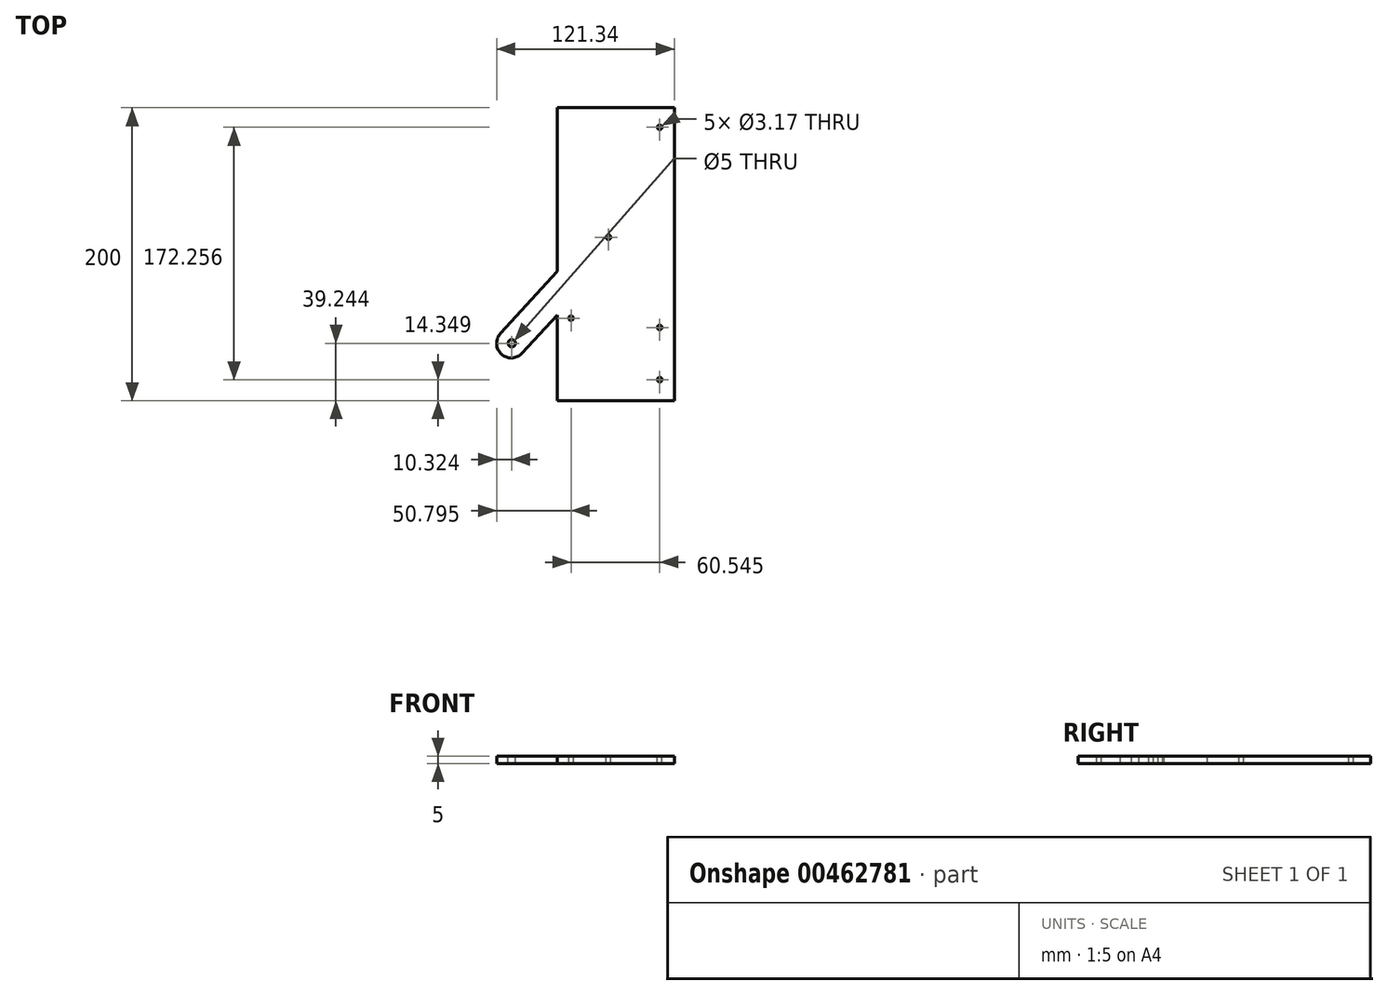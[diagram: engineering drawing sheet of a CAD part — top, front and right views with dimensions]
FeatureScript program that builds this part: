
annotation { "Feature Type Name" : "Feature", "Feature Type Description" : "" }
export const myFeature = defineFeature(function(context is Context, id is Id, definition is map)
    precondition{}
    {
        {
            var Q0;
            Q0=qCreatedBy(makeId("Top.planeOp"),FACE);
            var sketch = newSketch(context, id + "F0", { "sketchPlane" : qUnion([Q0])});
            skLineSegment(sketch, "E0.bottom", {"start": v(100, 150) * mm, "end": v(-100, 150) * mm});
            skLineSegment(sketch, "E0.top", {"start": v(100, -150) * mm, "end": v(-100, -150) * mm});
            skLineSegment(sketch, "E0.left", {"start": v(100, 150) * mm, "end": v(100, -150) * mm});
            skLineSegment(sketch, "E0.right", {"start": v(-100, 150) * mm, "end": v(-100, -150) * mm});
            skPoint(sketch, "E0.middle", {"position": v(0, 0) * mm});
            skSolve(sketch);
        }
        {
            var Q0;
            Q0=qSketchRegion(id+"F0",true);
            extrude(context, id + "F1", {"entities" : qUnion([Q0]), "depth" : 5 * mm});
        }
        {
            var Q0;
            Q0=makeQuery(id+"F1.opExtrude","CAP_FACE",FACE,{"disambiguationData":[OSD([sQuery(id+"F0.wireOp",EDGE,"E0.bottom"),sQuery(id+"F0.wireOp",EDGE,"E0.top"),sQuery(id+"F0.wireOp",EDGE,"E0.left"),sQuery(id+"F0.wireOp",EDGE,"E0.right")])],"isStart":false});
            var sketch = newSketch(context, id + "F2", { "sketchPlane" : qUnion([Q0])});
            skCircle(sketch, "E1", {"center": v(0, 0) * mm, "radius": 1.59 * mm});
            skCircle(sketch, "E2", {"center": v(0, -35.65) * mm, "radius": 1.59 * mm});
            skCircle(sketch, "E3", {"center": v(-60.54, 6.35) * mm, "radius": 1.59 * mm});
            skCircle(sketch, "E4", {"center": v(-35, 61.6) * mm, "radius": 1.59 * mm});
            skCircle(sketch, "E5", {"center": v(0, 136.6) * mm, "radius": 1.59 * mm});
            skLineSegment(sketch, "E6", {"start": v(0, 0) * mm, "end": v(-73.74, 0) * mm, "construction": true});
            skSolve(sketch);
        }
        {
            var Q0;
            Q0 = qSketchRegion(id + "F2", true);
            extrude(context, id + "F3", {"entities" : qUnion([Q0]), "operationType" : NewBodyOperationType.REMOVE, "endBound" : BoundingType.THROUGH_ALL, "oppositeDirection" : true, "depth" : 25 * mm});
        }
        {
            var Q0;
            Q0=makeQuery(id+"F1.opExtrude","CAP_FACE",FACE,{"disambiguationData":[OSD([sQuery(id+"F0.wireOp",EDGE,"E0.bottom"),sQuery(id+"F0.wireOp",EDGE,"E0.top"),sQuery(id+"F0.wireOp",EDGE,"E0.left"),sQuery(id+"F0.wireOp",EDGE,"E0.right")])],"isStart":false});
            var sketch = newSketch(context, id + "F4", { "sketchPlane" : qUnion([Q0])});
            skLineSegment(sketch, "E7.bottom", {"start": v(-70, 150) * mm, "end": v(10, 150) * mm});
            skLineSegment(sketch, "E7.top", {"start": v(-70, -50) * mm, "end": v(10, -50) * mm});
            skLineSegment(sketch, "E7.left", {"start": v(-70, 150) * mm, "end": v(-70, -50) * mm});
            skLineSegment(sketch, "E7.right", {"start": v(10, 150) * mm, "end": v(10, -50) * mm});
            skLineSegment(sketch, "E8.bottom", {"start": v(-100, 150) * mm, "end": v(100, 150) * mm});
            skLineSegment(sketch, "E8.top", {"start": v(-100, -150) * mm, "end": v(100, -150) * mm});
            skLineSegment(sketch, "E8.left", {"start": v(-100, 150) * mm, "end": v(-100, -150) * mm});
            skLineSegment(sketch, "E8.right", {"start": v(100, 150) * mm, "end": v(100, -150) * mm});
            skSolve(sketch);
        }
        {
            var Q0;
            Q0=makeQuery(id+"F4.imprint","IMPRINT",FACE,{"disambiguationData":[TD([[makeQuery(id+"F4.imprint","IMPRINT",EDGE,{"derivedFrom":sQuery(id+"F4.wireOp",EDGE,"E7.top")}),-1.0]])]});
            var Q1;
            Q1=makeQuery(id+"F4.imprint","IMPRINT",FACE,{"disambiguationData":[TD([[makeQuery(id+"F4.imprint","IMPRINT",EDGE,{"derivedFrom":makeQuery(id+"F3.boolean.opBoolean","COPY",EDGE,{"derivedFrom":makeQuery(id+"F3.opExtrude","CAP_EDGE",EDGE,{"disambiguationData":[OSD([sQuery(id+"F2.wireOp",EDGE,"E1")])],"isStart":true})})}),1.0]])]});
            var Q2;
            Q2=makeQuery(id+"F4.imprint","IMPRINT",FACE,{"disambiguationData":[TD([[makeQuery(id+"F4.imprint","IMPRINT",EDGE,{"derivedFrom":makeQuery(id+"F3.boolean.opBoolean","COPY",EDGE,{"derivedFrom":makeQuery(id+"F3.opExtrude","CAP_EDGE",EDGE,{"disambiguationData":[OSD([sQuery(id+"F2.wireOp",EDGE,"E2")])],"isStart":true})})}),1.0]])]});
            var Q3;
            Q3=makeQuery(id+"F4.imprint","IMPRINT",FACE,{"disambiguationData":[TD([[makeQuery(id+"F4.imprint","IMPRINT",EDGE,{"derivedFrom":makeQuery(id+"F3.boolean.opBoolean","COPY",EDGE,{"derivedFrom":makeQuery(id+"F3.opExtrude","CAP_EDGE",EDGE,{"disambiguationData":[OSD([sQuery(id+"F2.wireOp",EDGE,"E3")])],"isStart":true})})}),1.0]])]});
            var Q4;
            Q4=makeQuery(id+"F4.imprint","IMPRINT",FACE,{"disambiguationData":[TD([[makeQuery(id+"F4.imprint","IMPRINT",EDGE,{"derivedFrom":makeQuery(id+"F3.boolean.opBoolean","COPY",EDGE,{"derivedFrom":makeQuery(id+"F3.opExtrude","CAP_EDGE",EDGE,{"disambiguationData":[OSD([sQuery(id+"F2.wireOp",EDGE,"E4")])],"isStart":true})})}),1.0]])]});
            var Q5;
            Q5=makeQuery(id+"F4.imprint","IMPRINT",FACE,{"disambiguationData":[TD([[makeQuery(id+"F4.imprint","IMPRINT",EDGE,{"derivedFrom":makeQuery(id+"F3.boolean.opBoolean","COPY",EDGE,{"derivedFrom":makeQuery(id+"F3.opExtrude","CAP_EDGE",EDGE,{"disambiguationData":[OSD([sQuery(id+"F2.wireOp",EDGE,"E5")])],"isStart":true})})}),1.0]])]});
            extrude(context, id + "F5", {"entities" : qUnion([Q0, Q1, Q2, Q3, Q4, Q5]), "operationType" : NewBodyOperationType.REMOVE, "oppositeDirection" : true, "depth" : 25 * mm});
        }
        {
            var Q0;
            Q0=makeQuery(id+"F1.opExtrude","CAP_FACE",FACE,{"disambiguationData":[OSD([sQuery(id+"F0.wireOp",EDGE,"E0.bottom"),sQuery(id+"F0.wireOp",EDGE,"E0.top"),sQuery(id+"F0.wireOp",EDGE,"E0.left"),sQuery(id+"F0.wireOp",EDGE,"E0.right")])],"isStart":false});
            var sketch = newSketch(context, id + "F6", { "sketchPlane" : qUnion([Q0])});
            skLineSegment(sketch, "E9", {"start": v(-35, 61.6) * mm, "end": v(-35, -119.65) * mm});
            skLineSegment(sketch, "E10", {"start": v(-35, -119.65) * mm, "end": v(-35, 61.6) * mm});
            skLineSegment(sketch, "E11", {"start": v(0, 135.02) * mm, "end": v(0, 0) * mm});
            skLineSegment(sketch, "E12", {"start": v(-35, 61.6) * mm, "end": v(0, 99.8) * mm});
            skLineSegment(sketch, "E13", {"start": v(-35, 61.6) * mm, "end": v(-60.54, 6.35) * mm});
            skLineSegment(sketch, "E14", {"start": v(0, 99.8) * mm, "end": v(-101.34, -10.8) * mm});
            skArc(sketch, "E15.0.startCap", {"start": v(-7.37, 106.56) * mm, "mid": v(6.76, 107.17) * mm, "end": v(7.37, 93.05) * mm});
            skArc(sketch, "E15.0.endCap", {"start": v(-93.97, -17.55) * mm, "mid": v(-108.1, -18.16) * mm, "end": v(-108.71, -4.03) * mm});
            skLineSegment(sketch, "E15.0.left", {"start": v(7.37, 93.05) * mm, "end": v(-93.97, -17.55) * mm});
            skLineSegment(sketch, "E15.0.right", {"start": v(-7.37, 106.56) * mm, "end": v(-108.71, -4.03) * mm});
            skCircle(sketch, "E16", {"center": v(-35, 61.6) * mm, "radius": 1.59 * mm});
            skSolve(sketch);
        }
        {
            var Q0;
            Q0 = qSketchRegion(id + "F6", true);
            extrude(context, id + "F7", {"entities" : qUnion([Q0]), "operationType" : NewBodyOperationType.ADD, "oppositeDirection" : true, "depth" : 5 * mm});
        }
        {
            var Q0;
            Q0=makeQuery(id+"F7.boolean.opBoolean","MERGE",FACE,{"derivedFrom":[makeQuery(id+"F1.opExtrude","CAP_FACE",FACE,{"disambiguationData":[OSD([sQuery(id+"F0.wireOp",EDGE,"E0.bottom"),sQuery(id+"F0.wireOp",EDGE,"E0.top"),sQuery(id+"F0.wireOp",EDGE,"E0.left"),sQuery(id+"F0.wireOp",EDGE,"E0.right")])],"isStart":false}),makeQuery(id+"F7.opExtrude","CAP_FACE",FACE,{"disambiguationData":[OSD([sQuery(id+"F6.wireOp",EDGE,"E15.0.startCap"),sQuery(id+"F6.wireOp",EDGE,"E15.0.endCap"),sQuery(id+"F6.wireOp",EDGE,"E15.0.left"),sQuery(id+"F6.wireOp",EDGE,"E15.0.right"),sQuery(id+"F6.wireOp",EDGE,"E16")])],"isStart":true})]});
            var sketch = newSketch(context, id + "F8", { "sketchPlane" : qUnion([Q0])});
            skCircle(sketch, "E17", {"center": v(-101.02, -10.76) * mm, "radius": 2.5 * mm});
            skCircle(sketch, "E18", {"center": v(-101.34, -10.8) * mm, "radius": 10 * mm});
            skPoint(sketch, "E18.first.point", {"position": v(-108.71, -4.03) * mm});
            skPoint(sketch, "E18.second.point", {"position": v(-93.97, -17.55) * mm});
            skPoint(sketch, "E18.third.point.positionSnap0", {"position": v(-108.1, -18.16) * mm});
            skSolve(sketch);
        }
        {
            var Q0;
            Q0=makeQuery(id+"F8.imprint","IMPRINT",FACE,{"disambiguationData":[TD([[makeQuery(id+"F8.imprint","IMPRINT",EDGE,{"derivedFrom":sQuery(id+"F8.wireOp",EDGE,"E17")}),1.0]])]});
            extrude(context, id + "F9", {"entities" : qUnion([Q0]), "operationType" : NewBodyOperationType.REMOVE, "oppositeDirection" : true, "depth" : 25 * mm});
        }
    });
